# Revit family: Deca_Torneira lavatório mesa bica baixa_Unic_1785.90.SNS
name_source: partatom
category: Plumbing Fixtures
units: mm (PartAtom-declared; Revit-internal decimal feet)

## family parameters
Cut with Voids When Loaded = No
Host = Face
Part Type = Normal
Room Calculation Point = No
Round Connector Dimension = Use Radius
Shared = No

## types (3) — shared parameters
Acompanha o Produto = Acompanha 4 pilhas AA + Parfuso e bucha para fixação + Deca confort
Aprovado por = quattroD
Atendimento ao Cliente = 0800-0117073
Categoria = METAIS PARA BANHEIRO
Composição Anel Vedação = -
Composição Assento = -
Composição Básica = Liga de Cobre (bronze e latão),Plásticos de Engenharia,Elastômeros,Eletrônicos
Composição Componente = -
Consumo = -
Cor Interna = -
Cores Componente = -
Criado por = quattroD
Código Pai = 1785.90.SNS
Description = Torneira de mesa Touchless bica baixa para lavatório
Diâmetro Água Fria = 15 mm  [stored 0.0492126 ft]
Informações Complementares = -
Itens de Instalação = -
Manufacturer = Deca
Norma = NBR9050
Pressão máx. funcionamento = 40 MCA
Pressão mín. Aquec. Acúmulo = -
Pressão mín. Aquec. Passagem = -
Pressão mín. funcionamento = 2 MCA
Raio Água Fria = 8 mm  [stored 0.0262467 ft]
Saída de Esgoto = -
Segmento = Banheiro Luxo
Tipo de dispositivo economizador = Sim
Tipo de mecanismo utilizado = Solenóide
Tipo de rosca de entrada = BSP NBR 8133
Tipo de rosca de saída = -
URL = www.deca.com.br
Vazão na Pressão máx. (L/min) = 6
Vazão na Pressão mín. (L/min) = 4
zero-valued in all types: Default Elevation

## per-type parameters (varying)
| type | Cor Principal | Cor Secundária | Linha | Material | Model | Peso Líquido (Kg) |
| 1785.BL90.MT.SNS_Black Matte | Black Matte | Não Possui | Unic | Deca_Black Matte | 1785.BL90.MT.SNS | 1.726 |
| 1785.C90.SNS_Cromado | Cromado | - | Tube | Deca_Cromado | 1785.C90.SNS | 1.865 |
| 1785.GL90.RD.SNS_Gold Matte | Gold Matte | Não Possui | Tube | Deca_Gold Matte | 1785.GL90.RD.SNS | 1.726 |

note: source unit labels omitted for Vazão na Pressão máx. (L/min), Vazão na Pressão mín. (L/min) — the stored unit's dimension contradicts the parameter name (converter mislabeling)

note: [stored X ft] marks values corroborated as IEEE doubles in the binary element streams (Revit-internal decimal feet)

## geometry (parser evidence)
native form markers: Sweep x3
no freeform markers — native parametric forms only
